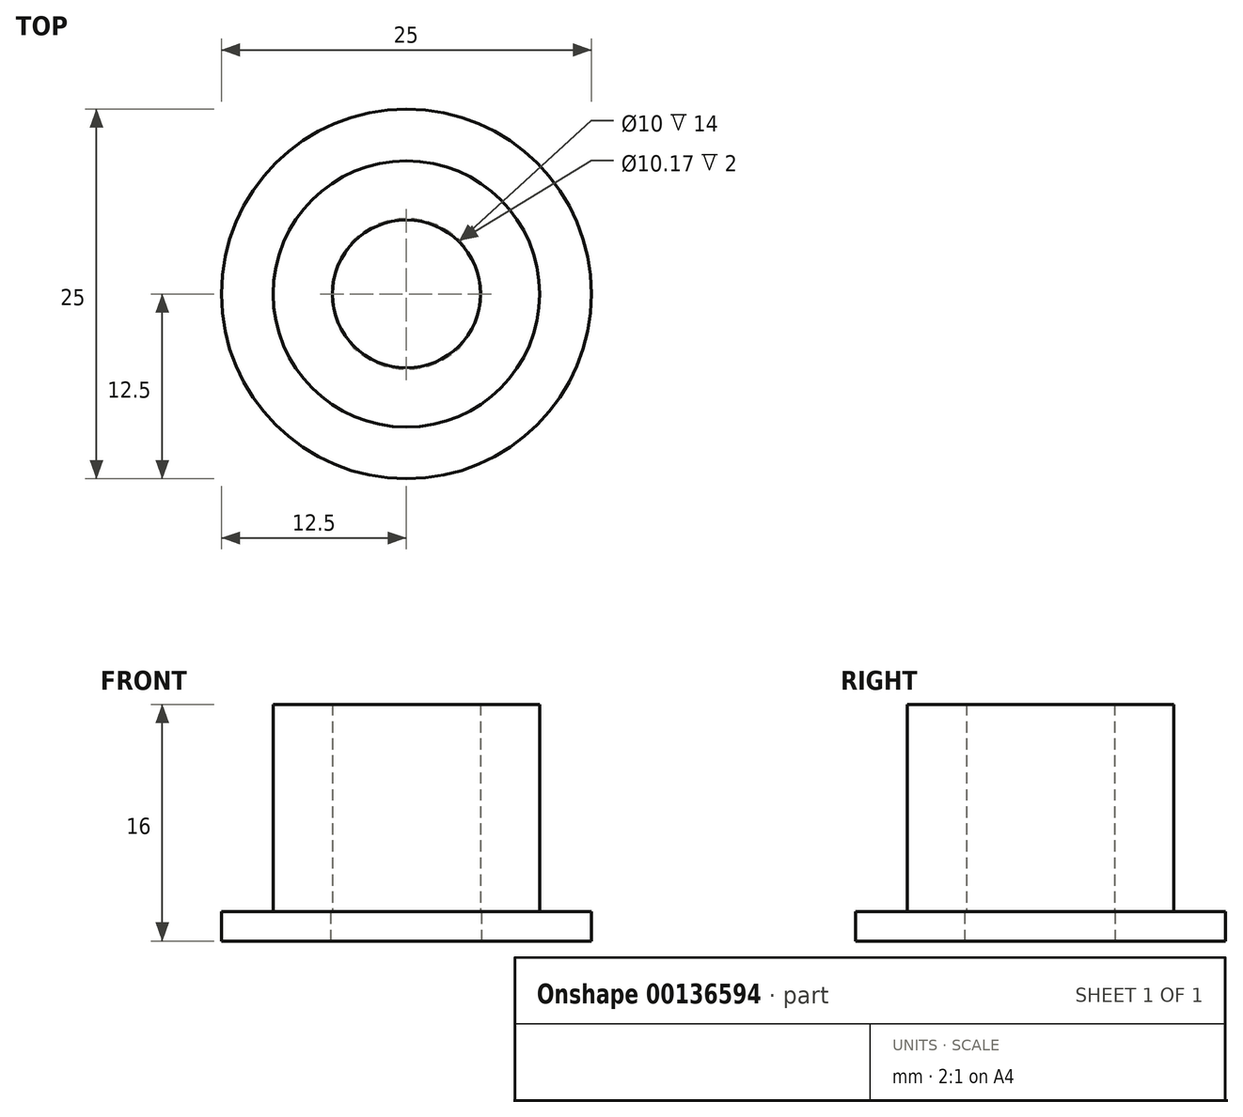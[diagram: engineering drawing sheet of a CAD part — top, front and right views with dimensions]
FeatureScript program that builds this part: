
annotation { "Feature Type Name" : "Feature", "Feature Type Description" : "" }
export const myFeature = defineFeature(function(context is Context, id is Id, definition is map)
    precondition{}
    {
        {
            var Q0;
            Q0=qCreatedBy(makeId("Top.planeOp"),FACE);
            var sketch = newSketch(context, id + "F0", { "sketchPlane" : qUnion([Q0])});
            skCircle(sketch, "E0", {"center": v(0, 0) * mm, "radius": 9 * mm});
            skCircle(sketch, "E1", {"center": v(0, 0) * mm, "radius": 5 * mm});
            skSolve(sketch);
        }
        {
            var Q0;
            Q0 = qSketchRegion(id + "F0", true);
            extrude(context, id + "F1", {"entities" : qUnion([Q0]), "depth" : 14 * mm});
        }
        {
            var Q0;
            Q0=qCreatedBy(makeId("Top.planeOp"),FACE);
            var sketch = newSketch(context, id + "F2", { "sketchPlane" : qUnion([Q0])});
            skCircle(sketch, "E2", {"center": v(0, 0) * mm, "radius": 12.5 * mm});
            skCircle(sketch, "E3", {"center": v(0, 0) * mm, "radius": 5.08 * mm});
            skSolve(sketch);
        }
        {
            var Q0;
            Q0 = qSketchRegion(id + "F2", true);
            extrude(context, id + "F3", {"entities" : qUnion([Q0]), "operationType" : NewBodyOperationType.ADD, "oppositeDirection" : true, "depth" : 2 * mm});
        }
    });
